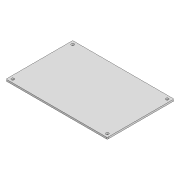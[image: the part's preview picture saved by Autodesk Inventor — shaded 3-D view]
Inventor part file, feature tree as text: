
AUTODESK INVENTOR PART (.ipt)
format: ipt  version: 2020 (Build 240168000, 168)  size: 111,616 bytes
history: native  units: mm
features: extrude x2, sketch x2, other x1, fillet x1
ambient origin geometry x8: Origin, YZ Plane, XZ Plane, XY Plane, X Axis, Y Axis, Z Axis, Center Point
bodies: Body1 (feature_tree)
feature tree (6):
  other  "Sólido1"
  extrude  "Extrusão1"  Depth=158.0mm
  fillet  "Arredondamento1"  Radius=4.0mm
  extrude  "Extrusão2"  Depth=10.0mm
  sketch  "Esboço1"  dims[d0=240.0mm d1=158.0mm d2=4.0mm d3=0.0mm]
  sketch  "Esboço2"  dims[d4=2.0mm d5=6.7mm d6=6.7mm d7=6.7mm d8=6.7mm d9=8.0mm d10=8.0mm d11=8.0mm d12=8.0mm d13=8.0mm d14=8.0mm d15=8.0mm d16=8.0mm d17=10.0mm d18=0.0mm]
